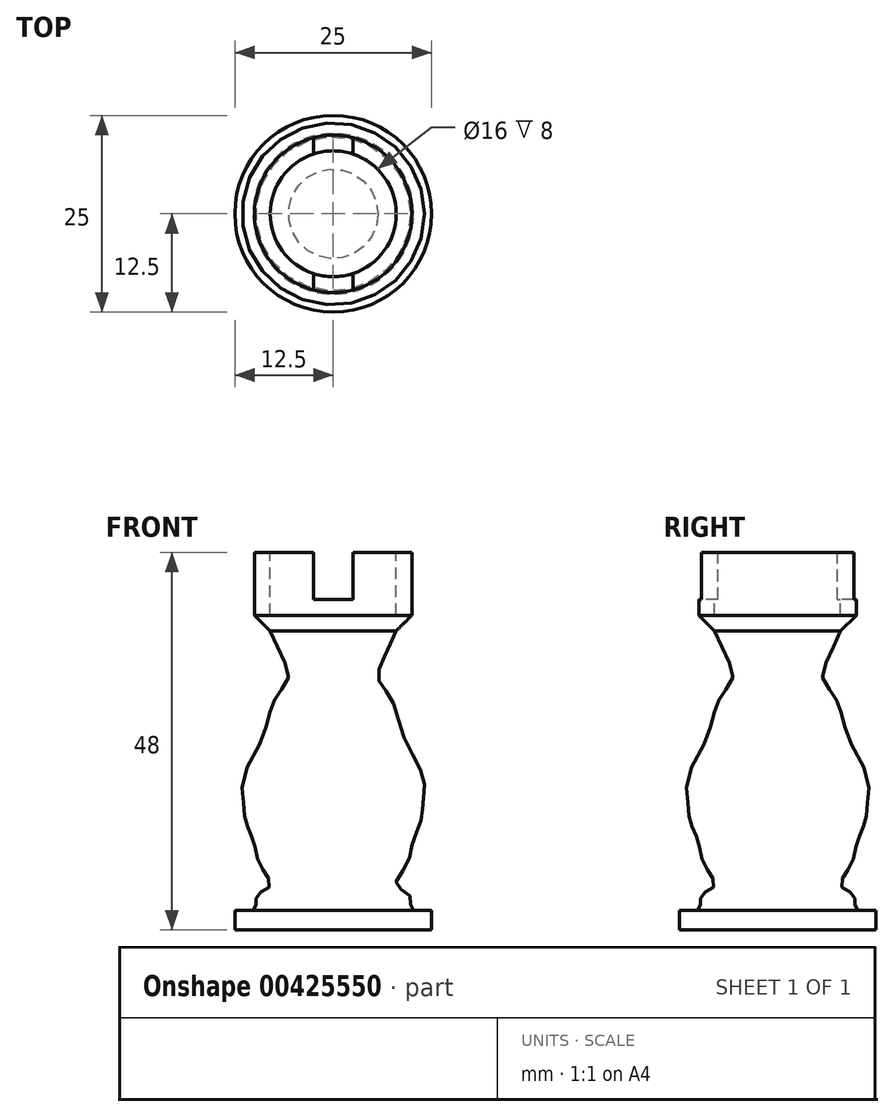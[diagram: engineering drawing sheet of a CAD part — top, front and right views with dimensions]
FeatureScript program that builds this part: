
annotation { "Feature Type Name" : "Feature", "Feature Type Description" : "" }
export const myFeature = defineFeature(function(context is Context, id is Id, definition is map)
    precondition{}
    {
        {
            var Q0;
            Q0=qCreatedBy(makeId("Front.planeOp"),FACE);
            var sketch = newSketch(context, id + "F0", { "sketchPlane" : qUnion([Q0])});
            skLineSegment(sketch, "E0.bottom", {"start": v(0, 0) * mm, "end": v(12.5, 0) * mm});
            skLineSegment(sketch, "E0.top", {"start": v(0, 48) * mm, "end": v(12.5, 48) * mm});
            skLineSegment(sketch, "E0.left", {"start": v(0, 0) * mm, "end": v(0, 48) * mm});
            skLineSegment(sketch, "E0.right", {"start": v(12.5, 0) * mm, "end": v(12.5, 48) * mm});
            skLineSegment(sketch, "E1.bottom", {"start": v(0, 48) * mm, "end": v(8, 48) * mm});
            skLineSegment(sketch, "E1.top", {"start": v(0, 40) * mm, "end": v(8, 40) * mm});
            skLineSegment(sketch, "E1.left", {"start": v(0, 48) * mm, "end": v(0, 40) * mm});
            skLineSegment(sketch, "E1.right", {"start": v(8, 48) * mm, "end": v(8, 40) * mm});
            skLineSegment(sketch, "E2", {"start": v(10, 48) * mm, "end": v(10, 38) * mm});
            skLineSegment(sketch, "E3", {"start": v(10, 38) * mm, "end": v(0, 38) * mm});
            skLineSegment(sketch, "E4", {"start": v(10, 40) * mm, "end": v(8, 38) * mm});
            skLineSegment(sketch, "E5", {"start": v(0, 2.5) * mm, "end": v(12.5, 2.5) * mm});
            skFitSpline(sketch, "E6", {"points": [v(8, 38) * mm, v(6.53, 34.84) * mm, v(5.72, 31.92) * mm, v(7.3, 29.57) * mm, v(8.98, 24.49) * mm, v(11.42, 19.45) * mm, v(11.42, 16.31) * mm, v(11.2, 14.02) * mm, v(10.12, 11.27) * mm, v(9.28, 8.22) * mm, v(8, 5.7) * mm, v(9.67, 4.47) * mm, v(9.82, 3.17) * mm, v(10.2, 2.5) * mm], "startDerivative": vector(-16.71, -36.46) * mm, "endDerivative": vector(12.9, -14.34) * mm});
            skSolve(sketch);
        }
        {
            var Q0;
            {var subQ0=sQuery(id+"F0.wireOp",EDGE,"E1.top");Q0=makeQuery(id+"F0.imprint","IMPRINT",FACE,{"disambiguationData":[TD([[makeQuery(id+"F0.imprint","IMPRINT",EDGE,{"derivedFrom":subQ0}),-1.0]])]});}
            var Q1;
            {var subQ5=sQuery(id+"F0.wireOp",EDGE,"E6");Q1=makeQuery(id+"F0.imprint","IMPRINT",FACE,{"disambiguationData":[TD([[makeQuery(id+"F0.imprint","IMPRINT",EDGE,{"derivedFrom":subQ5}),-1.0]])]});}
            var Q2;
            {var subQ5=sQuery(id+"F0.wireOp",EDGE,"E0.bottom");Q2=makeQuery(id+"F0.imprint","IMPRINT",FACE,{"disambiguationData":[TD([[makeQuery(id+"F0.imprint","IMPRINT",EDGE,{"derivedFrom":subQ5}),1.0]])]});}
            var Q3;
            Q3=sQuery(id+"F0.wireOp",EDGE,"E1.left");
            revolve(context, id + "F1", {"entities" : qUnion([Q0, Q1, Q2]), "axis" : qUnion([Q3]), "revolveType" : RevolveType.FULL});
        }
        {
            var Q0;
            Q0=makeQuery(id+"F1.opRevolve","SWEPT_FACE",FACE,{"disambiguationData":[OSD([sQuery(id+"F0.wireOp",EDGE,"E0.top")])]});
            var sketch = newSketch(context, id + "F2", { "sketchPlane" : qUnion([Q0])});
            skLineSegment(sketch, "E7.bottom", {"start": v(-2.5, 15) * mm, "end": v(2.5, 15) * mm});
            skLineSegment(sketch, "E7.top", {"start": v(-2.5, -15) * mm, "end": v(2.5, -15) * mm});
            skLineSegment(sketch, "E7.left", {"start": v(-2.5, 15) * mm, "end": v(-2.5, -15) * mm});
            skLineSegment(sketch, "E7.right", {"start": v(2.5, 15) * mm, "end": v(2.5, -15) * mm});
            skPoint(sketch, "E7.middle", {"position": v(0, 0) * mm});
            skSolve(sketch);
        }
        {
            var Q0;
            Q0 = qSketchRegion(id + "F2", true);
            extrude(context, id + "F3", {"entities" : qUnion([Q0]), "operationType" : NewBodyOperationType.REMOVE, "oppositeDirection" : true, "depth" : 6 * mm});
        }
    });
